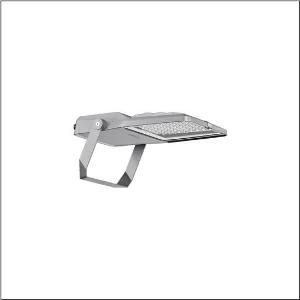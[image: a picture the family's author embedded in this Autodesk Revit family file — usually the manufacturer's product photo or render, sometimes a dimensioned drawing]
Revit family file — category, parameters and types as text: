
# Revit family: floodlight_fl_21_mini___pl33t_5xa7776d2f1a_88fb
name_source: partatom
category: Lighting Fixtures
units: mm (PartAtom-declared; Revit-internal decimal feet)

## family parameters
Cut with Voids When Loaded = No
Host = Face
Light Source = No
Part Type = Normal
Room Calculation Point = No
Round Connector Dimension = Use Diameter
Shared = No

## types (1)
- --- (1 x LED, 17630 lm, 142.9 W, 3000K)
    Apparent Load = 143 VA
    CIE Flux Codes = 26 75 99 100 100
    Color Rendering = 70
    Color Temperature = 3000K
    Default Elevation = 1800 mm
    Description = Floodlight FL 21 mini, floodlight, primary light control with lens, of PMMA, primary optical cover: protective disc, of toughened safety glass, transparent, light distribution: PL33T, light emission: direct distribution, installation type: surface-mounted, LED, High Power LED, rated luminous flux: 17.630lm, luminous efficacy: 123lm/W, light colour: 730, colour temperature: 3000K, control: flexible luminous flux parameterisation, time-dependent luminous flux control, constant luminous flux control, overheat protection, presetting dimming logarithmic, with terminal, 6-pole, mains connection: 220..240V, AC, 50/60Hz, start of lifetime: 143W, end of service life: 151W, reduction: 63W, luminaire housing, of diecast aluminium, powder-coated, Siteco® metallic grey (DB 702S), corrosivity category C5 mid according to DIN EN ISO 12944, sealing non-destructively replaceable, mounting bracket, of steel, galvanised, powder-coated, Siteco® metallic grey (DB 702S), Smart Interface below and above, protection rating (complete): IP66, insulation class (complete): insulation class II (safety insulation), certification: CE, ENEC, VDE, protection symbol: D, impact resistance: IK08, permissible operating ambient temperature: -40..+40°C, permissible operating ambient temperature for outdoor applications: -40..+50°C, standard: DIN EN 12944, LABS conformity tested according to VDMA 24364:2018-05, packaging unit: 1 piece

Light Distribution: PL33T
    Height = 70 mm
    Lamp = 1 x LED
    Lamp Light Flux = 17630 lm
    Lamp Power = 142.9 W
    Lamp count = 1
    Length = 485 mm
    Luminous efficacy = 123 lm/W
    Manufacturer = Siteco
    ModVariant = No
    Model = 5XA7776D2F1A
    Number of Poles = 1
    OnlyDefault = Yes
    Power Factor = 1
    Product Name = Floodlight FL 21 mini | PL33T
    Product group = floodlight | pylon annexe
    ProductGroupID = 6200
    Protection Class = Protection class II
    Protection Degree = IP 66
    RLX_Detail_Level = 1
    RLX_Emergency_Light_Flux = 0 lm
    RLX_Emergency_Type = 0
    RLX_Emergency_Type_DB = No
    RlxData = <blob elided: 96029 chars, md5=cfece336>
    Socket = socket
    Standby Power = 0 W
    System Light Flux = 17630 lm
    System Power = 143 W
    Type Comments = factory setting: luminous flux: 100 % | dim-lin: 254 | 730 mA
    Type Image = l_1006845.jpg
    URL = http://relux.com
    VarID = @adj_098527
    Voltage = 0 V
    Weight = 0.00 kg
    Width = 337 mm

## geometry (parser evidence)
native form markers: Blend x4, Sweep x14
no freeform markers — native parametric forms only
